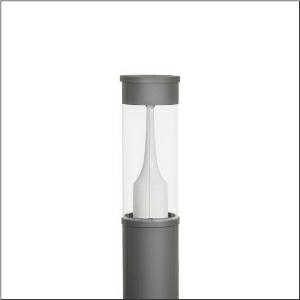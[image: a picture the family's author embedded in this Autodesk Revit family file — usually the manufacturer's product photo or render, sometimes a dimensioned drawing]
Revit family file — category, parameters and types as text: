
# Revit family: city-light_120_iq___p1_0a_5xa5285nf14h_00f5
name_source: partatom
category: Lighting Fixtures
units: mm (PartAtom-declared; Revit-internal decimal feet)

## family parameters
Cut with Voids When Loaded = No
Host = Face
Light Source = No
Part Type = Normal
Room Calculation Point = No
Round Connector Dimension = Use Diameter
Shared = No

## types (1)
- --- (1 x LED, 1510 lm, 11.8 W, 2700K)
    Apparent Load = 12 VA
    CIE Flux Codes = 32 61 90 93 100
    Color Rendering = 70
    Color Temperature = 2700K
    Default Elevation = 1800 mm
    Description = City-Light 120 iQ, bollard luminaire, Module 540 iQ-SR, primary light control with 3 zone facetted reflector, of plastic, silver coated, highly specular, structured, primary optical cover: cover, of PMMA, transparent, partly coated, light distribution: P1.0a, primary light characteristic: strongly asymmetric, LED, High Power LED, rated luminous flux: 1.510lm, luminous efficacy: 128lm/W, light colour: 727, colour temperature: 2700K, control gear: ECG iQ, control: presetting dimming logarithmic, Street-Remote, Auto-Match, Temp-Guard, Lumen-Switch, Night-Set, Smart-Wire, Light-Fading, Desk-Remote (wireless, voltage-free reading and setting of iQ features in the workshop via application-optimized NFC function/RFID function), optimised constant luminous flux control (CLO 2.0), with terminal, 6-pole, max. 2.5mm², mains connection: 220..240V, AC, 50/60Hz, start of lifetime: 12W, end of lifetime: 12W, reduction: 6W, luminaire housing, cylindrical, of extruded aluminium section, coated, Siteco® metallic grey (DB 702S), length: 1.200mm, diameter: 200mm, Module 540 iQ-SR, traffic white (RAL 9016), equipment: standard, protection rating (complete): IP54, insulation class (complete): insulation class II (safety insulation), certification: CE, ENEC, VDE, packaging unit: 1 piece

Light Distribution: P1.0a
    Height = 500 mm
    Lamp = 1 x LED
    Lamp Light Flux = 1510 lm
    Lamp Power = 11.8 W
    Lamp count = 1
    Length = 200 mm  [stored 0.656168 ft]
    Luminous efficacy = 128 lm/W
    Manufacturer = Siteco
    ModVariant = No
    Model = 5XA5285NF14H
    Number of Poles = 1
    OnlyDefault = Yes
    Power Factor = 1
    Product Name = City-Light 120 iQ | P1.0a
    Product group = bollard luminaire | pylon top
    ProductGroupID = 6104
    Protection Class = Protection class II
    Protection Degree = IP 54
    RLX_Detail_Level = 1
    RlxData = <blob elided: 52333 chars, md5=20a1bab3>
    Socket = socket
    Standby Power = 0 W
    System Light Flux = 1510 lm
    System Power = 12 W
    Type Comments = factory setting: luminous flux: 100 % | dim-lin: 254 | 472 mA
    Type Image = l_1006922.jpg
    URL = http://relux.com
    VarID = @adj_063025
    Voltage = 0 V
    Weight = 0.00 kg
    Width = 0 mm  [stored 0 ft]

note: [stored X ft] marks values corroborated as IEEE doubles in the binary element streams (Revit-internal decimal feet)

## geometry (parser evidence)
native form markers: Blend x4, Sweep x10
no freeform markers — native parametric forms only
